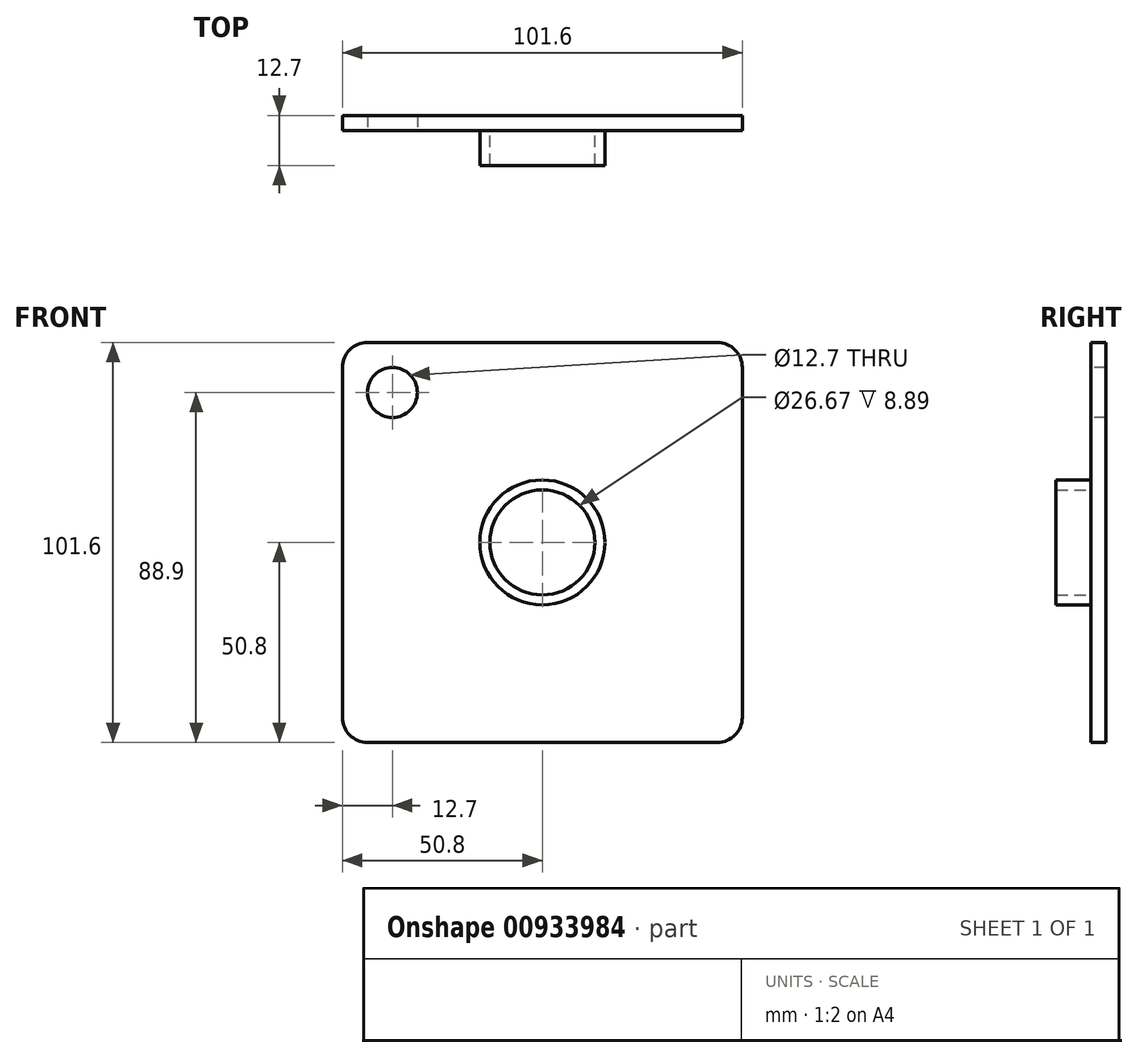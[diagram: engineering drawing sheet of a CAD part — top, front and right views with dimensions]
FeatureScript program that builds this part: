
annotation { "Feature Type Name" : "Feature", "Feature Type Description" : "" }
export const myFeature = defineFeature(function(context is Context, id is Id, definition is map)
    precondition{}
    {
        {
            var Q0;
            Q0=qCreatedBy(makeId("Front.planeOp"),FACE);
            var sketch = newSketch(context, id + "F0", { "sketchPlane" : qUnion([Q0])});
            skLineSegment(sketch, "E0.bottom", {"start": v(-44.45, 50.8) * mm, "end": v(44.45, 50.8) * mm});
            skLineSegment(sketch, "E0.top", {"start": v(-44.45, -50.8) * mm, "end": v(44.45, -50.8) * mm});
            skLineSegment(sketch, "E0.left", {"start": v(-50.8, 44.45) * mm, "end": v(-50.8, -44.45) * mm});
            skLineSegment(sketch, "E0.right", {"start": v(50.8, 44.45) * mm, "end": v(50.8, -44.45) * mm});
            skPoint(sketch, "E1.visualSharp", {"position": v(-50.8, 50.8) * mm});
            skArc(sketch, "E1.filletArc", {"start": v(-44.45, 50.8) * mm, "mid": v(-48.94, 48.94) * mm, "end": v(-50.8, 44.45) * mm});
            skPoint(sketch, "E2.visualSharp", {"position": v(50.8, 50.8) * mm});
            skArc(sketch, "E2.filletArc", {"start": v(50.8, 44.45) * mm, "mid": v(48.94, 48.94) * mm, "end": v(44.45, 50.8) * mm});
            skPoint(sketch, "E3.visualSharp", {"position": v(50.8, -50.8) * mm});
            skArc(sketch, "E3.filletArc", {"start": v(44.45, -50.8) * mm, "mid": v(48.94, -48.94) * mm, "end": v(50.8, -44.45) * mm});
            skPoint(sketch, "E4.visualSharp", {"position": v(-50.8, -50.8) * mm});
            skArc(sketch, "E4.filletArc", {"start": v(-50.8, -44.45) * mm, "mid": v(-48.94, -48.94) * mm, "end": v(-44.45, -50.8) * mm});
            skSolve(sketch);
        }
        {
            var Q0;
            Q0 = qSketchRegion(id + "F0", true);
            extrude(context, id + "F1", {"entities" : qUnion([Q0]), "depth" : 3.8 * mm, "offsetDistance" : 25.4 * mm});
        }
        {
            var Q0;
            Q0=qCreatedBy(makeId("Front.planeOp"),FACE);
            var sketch = newSketch(context, id + "F2", { "sketchPlane" : qUnion([Q0])});
            skCircle(sketch, "E5", {"center": v(-38.1, 38.1) * mm, "radius": 6.35 * mm});
            skSolve(sketch);
        }
        {
            var Q0;
            Q0 = qSketchRegion(id + "F2", true);
            extrude(context, id + "F3", {"entities" : qUnion([Q0]), "operationType" : NewBodyOperationType.REMOVE, "endBound" : BoundingType.THROUGH_ALL, "oppositeDirection" : true, "depth" : 25.4 * mm, "offsetDistance" : 25.4 * mm, "hasSecondDirection" : true, "secondDirectionOppositeDirection" : false, "secondDirectionDepth" : 25.4 * mm});
        }
        {
            var Q0;
            Q0=qCreatedBy(makeId("Front.planeOp"),FACE);
            var sketch = newSketch(context, id + "F4", { "sketchPlane" : qUnion([Q0])});
            skCircle(sketch, "E6", {"center": v(0, 0) * mm, "radius": 15.87 * mm});
            skCircle(sketch, "E7", {"center": v(0, 0) * mm, "radius": 13.34 * mm});
            skSolve(sketch);
        }
        {
            var Q0;
            Q0 = qSketchRegion(id + "F4", true);
            extrude(context, id + "F5", {"entities" : qUnion([Q0]), "operationType" : NewBodyOperationType.ADD, "depth" : 12.7 * mm, "offsetDistance" : 25.4 * mm});
        }
    });
